# Revit family: 22L-W-I
name_source: partatom
category: Lighting Fixtures
units: mm (PartAtom-declared; Revit-internal decimal feet)

## family parameters
Cut with Voids When Loaded = No
Host = Face
Light Source = Yes
OmniClass Number = 23.80.70.11.14.17
OmniClass Title = Direct/Indirect
Part Type = Normal
Room Calculation Point = No
Round Connector Dimension = Use Diameter
Shared = Yes

## types (4) — shared parameters
Apparent Load = 0 VA
Assembly Code = D5020200
Color Filter = 16777215
Default Elevation = 4' - 0"
Description = 22L Wall Indirect (22L-W-I) is a small-scale extruded aluminum fixture. Its small housing provides a clean, minimalist look in both small and large areas.
Dimming Lamp Color Temperature Shift = <None>
Emit Shape Visible in Rendering = No
Emit from Rectangle Length = 0' - 2"
Fixture Distribution = Indirect
Glass = Glass - White
Housing Material = Paint - Matte White
Lamp = LED
Load Classification = Lighting
Manufacturer = Litecontrol
Model = MOD 22L LED Wall Indirect
Mounting = Wall-Mount
Photometric Web File = generic.ies
Power Factor = 1
Tilt Angle = -90.00°
Type Comments = Lighting Fixture
URL = https://www.currentlighting.com
Voltage = 120 V
Warranty = 5-Years Warranty
zz YesNo 1 = No
zz YesNo 2 = Yes

## per-type parameters (varying)
| type | Emit from Rectangle Width | zz Length 1 |
| 22L-W-I-04 | 3' - 10" | 4' - 0" |
| 22L-W-I-03 | 2' - 10" | 3' - 0" |
| 22L-W-I-06 | 5' - 10" | 6' - 0" |
| 22L-W-I-08 | 7' - 10" | 8' - 0" |

## geometry (parser evidence)
native form markers: Sweep x6
no freeform markers — native parametric forms only
